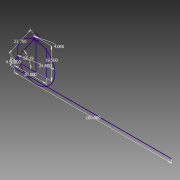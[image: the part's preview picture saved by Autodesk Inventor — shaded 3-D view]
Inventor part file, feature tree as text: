
AUTODESK INVENTOR PART (.ipt)
format: ipt  version: 2014 SP1 (Build 180222100, 222)  size: 71,680 bytes
history: native  units: in
note: dims shown in document units (in); Inventor stores cm internally (conversion verified against a paired STEP export)
features: sketch x1
ambient origin geometry x8: Origin, YZ Plane, XZ Plane, XY Plane, X Axis, Y Axis, Z Axis, Center Point
feature tree (1):
  sketch  "Sketch1"  dims[d5=1.0in d6=23.75in d8=20.0in d13=4.5in d14=100.0in d17=19.5in d21=4.0in d28=24.0in d29=0.3792in]
